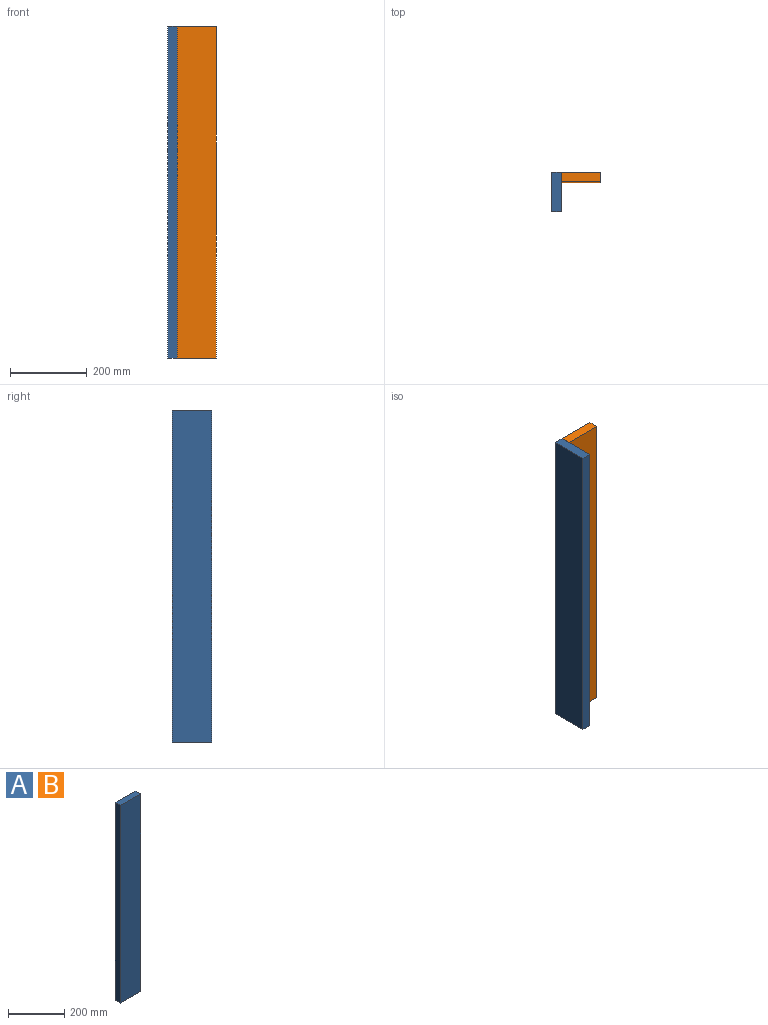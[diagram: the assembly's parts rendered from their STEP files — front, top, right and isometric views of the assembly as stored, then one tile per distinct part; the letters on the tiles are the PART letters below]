
ASSEMBLY  parts=2 mates=1
PART A: 6 faces, bbox 101.6x25.4x863.6 mm
  f0: plane 863.6x25.4mm, normal (-1,0,0), area 21935.4mm2, adj f1,f3,f4,f5
  f1: plane 863.6x101.6mm, normal (0,-1,0), area 87741.8mm2, adj f0,f2,f4,f5
  f2: plane 863.6x25.4mm, normal (1,0,0), area 21935.4mm2, adj f1,f3,f4,f5
  f3: plane 863.6x101.6mm, normal (0,1,0), area 87741.8mm2, adj f0,f2,f4,f5
  f4: plane 101.6x25.4mm, normal (0,0,1), area 2580.6mm2, adj f0,f1,f2,f3
  f5: plane 101.6x25.4mm, normal (0,0,-1), area 2580.6mm2, adj f0,f1,f2,f3
PART B: same geometry as A
PLACE A rot(axis=(0,0,1),90deg) t=(-148.06,72.57,-105.37)mm
PLACE B t=(-148.06,148.77,-105.37)mm
MATE fastened A.f1 <-> B.f0  axis (1,0,0) through (-148.06,174.17,326.43)mm
